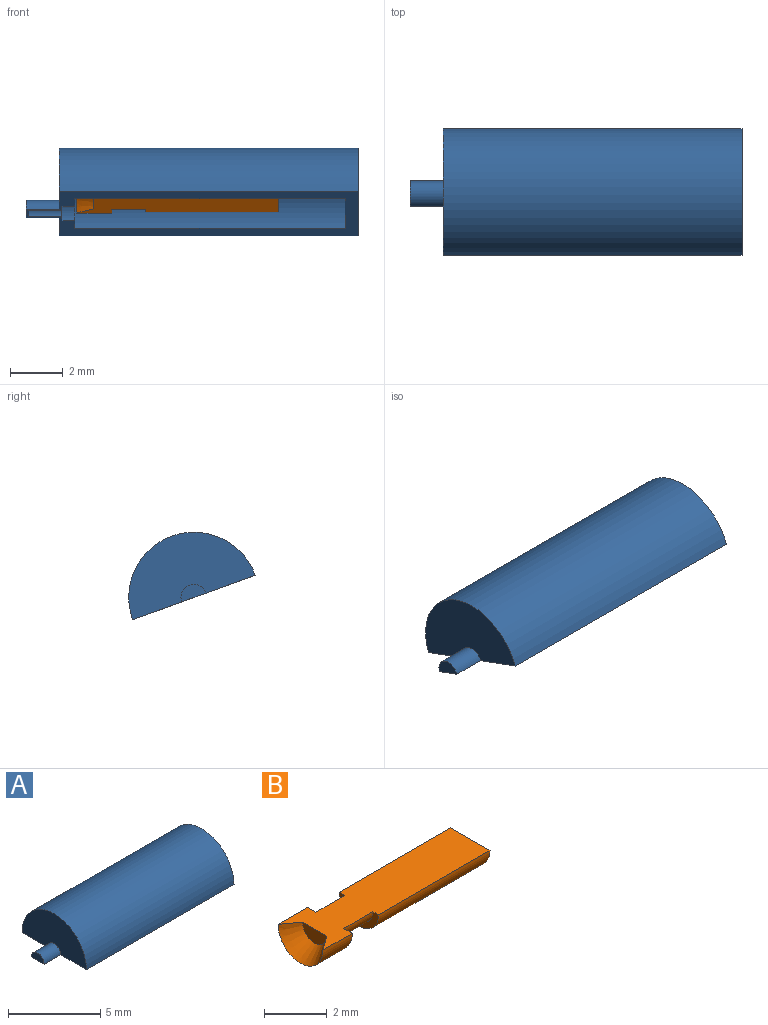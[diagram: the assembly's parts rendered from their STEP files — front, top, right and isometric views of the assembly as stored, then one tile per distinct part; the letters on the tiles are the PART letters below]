
ASSEMBLY  parts=2 mates=1
PART A: 13 faces, bbox 12.6x5x2.5 mm
  f0: cylinder r=2.48mm len=11.34mm, axis (-1,0,0), area 88.3mm2, adj f1,f11,f12
  f1: plane 4.96x2.48mm, normal (-1,0,0), area 9.3mm2, adj f0,f2,f12
  f2: cylinder r=0.49mm len=1.27mm, axis (-1,0,0), area 2mm2, adj f1,f3,f12
  f3: plane 0.99x0.49mm, normal (-1,0,0), area 0.4mm2, adj f2,f12
  f4: plane 0.65x0.32mm, normal (1,0,0), area 0.2mm2, adj f5,f12
  f5: cylinder r=0.32mm len=1.25mm, axis (-1,0,0), area 1.3mm2, adj f4,f6,f12
  f6: plane 1.64x0.82mm, normal (1,0,0), area 0.9mm2, adj f5,f7,f12
  f7: cylinder r=0.82mm len=1.64mm, axis (-1,0,0), area 1.3mm2, adj f6,f8,f12
  f8: plane 3.3x1.65mm, normal (1,0,0), area 3.2mm2, adj f7,f9,f12
  f9: cylinder r=1.65mm len=10.26mm, axis (-1,0,0), area 53.2mm2, adj f8,f10,f12
  f10: plane 3.3x1.65mm, normal (-1,0,0), area 4.3mm2, adj f9,f12
  f11: plane 4.96x2.48mm, normal (1,0,0), area 9.6mm2, adj f0,f12
  f12: plane 12.61x4.96mm, normal (0,0,-1), area 22mm2, adj f0,f1,f2,f3,f4,f5,f6,f7
PART B: 9 faces, bbox 7.7x2x1 mm
  f0: cone r=1.01mm half-angle=36deg, axis (-1,0,0), area 1.9mm2, adj f1,f7,f8
  f1: cylinder r=1.01mm len=2.02mm, axis (-1,0,0), area 4.2mm2, adj f0,f2,f8
  f2: plane 2.02x1.01mm, normal (1,0,0), area 1mm2, adj f1,f3,f8
  f3: cylinder r=0.63mm len=1.31mm, axis (-1,0,0), area 2.6mm2, adj f2,f4,f8
  f4: plane 1.77x0.88mm, normal (-1,0,0), area 0.6mm2, adj f3,f5,f8
  f5: cylinder r=0.88mm len=5.03mm, axis (-1,0,0), area 14mm2, adj f4,f6,f8
  f6: plane 1.77x0.88mm, normal (1,0,0), area 1.2mm2, adj f5,f8
  f7: plane 1.09x0.55mm, normal (-1,0,0), area 0.5mm2, adj f0,f8
  f8: plane 7.66x2.02mm, normal (0,0,1), area 12.2mm2, adj f0,f1,f2,f3,f4,f5,f6,f7
PLACE A rot(axis=(-1,0,0),20deg) t=(-1.46,39.17,-24.56)mm
PLACE B rot(axis=(1,0,0),160deg) t=(-1.55,32.49,-42.92)mm
MATE slider B.f0 <-> A.f6  axis (-1,0,0) through (113.29,35.9,-33.56)mm
